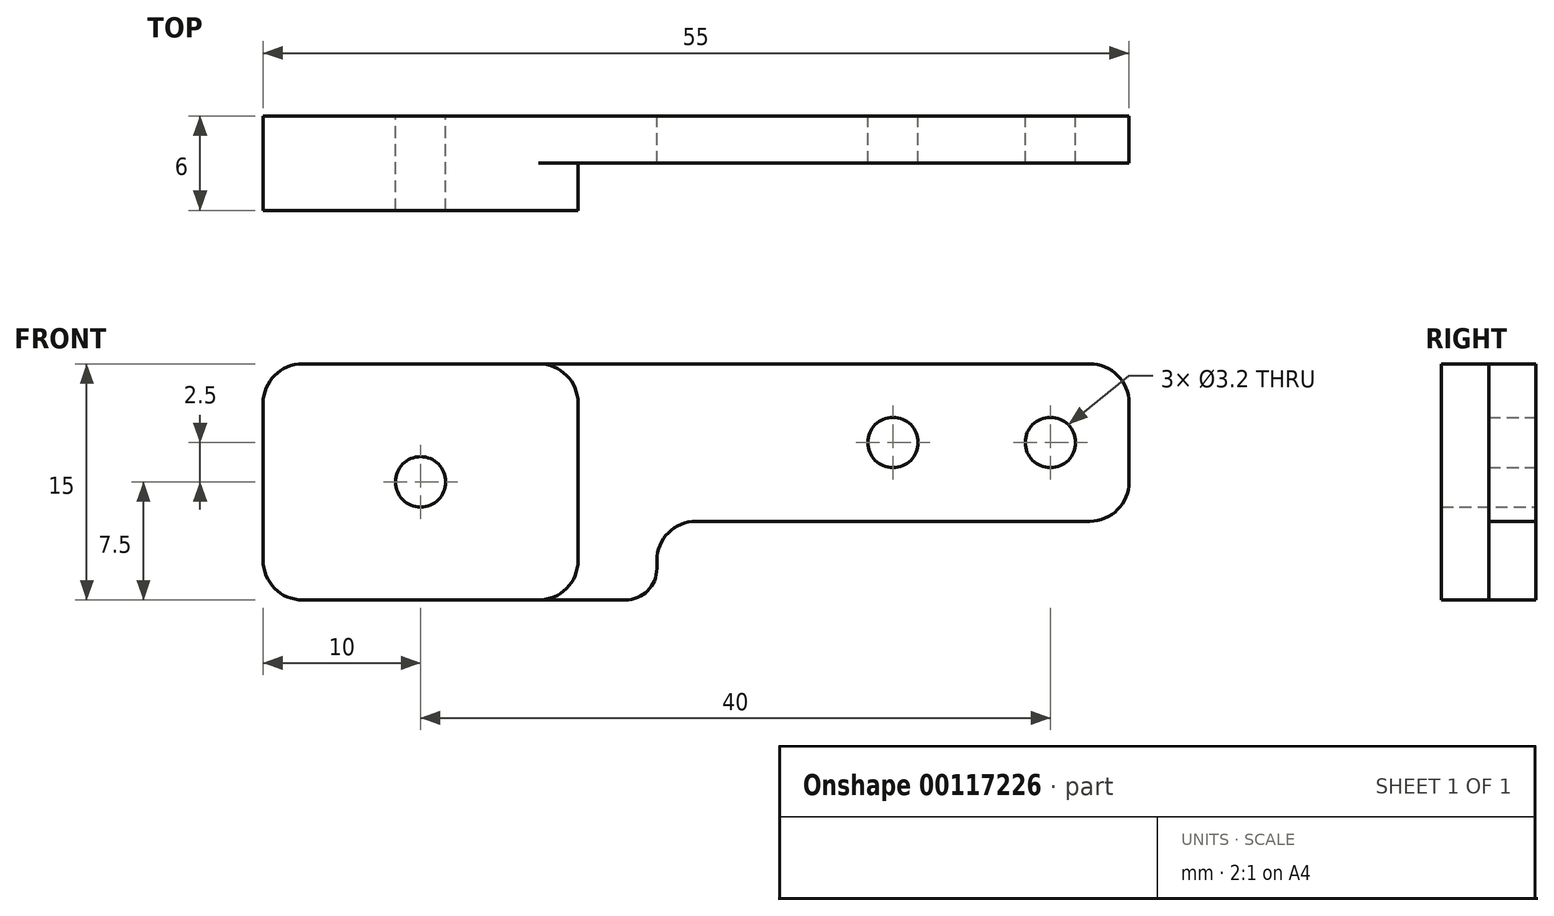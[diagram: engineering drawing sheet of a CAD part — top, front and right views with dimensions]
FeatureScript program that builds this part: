
annotation { "Feature Type Name" : "Feature", "Feature Type Description" : "" }
export const myFeature = defineFeature(function(context is Context, id is Id, definition is map)
    precondition{}
    {
        {
            var Q0;
            Q0=qCreatedBy(makeId("Front.planeOp"),FACE);
            var sketch = newSketch(context, id + "F0", { "sketchPlane" : qUnion([Q0])});
            skLineSegment(sketch, "E0.bottom", {"start": v(-4.5, -7.5) * mm, "end": v(-25, -7.5) * mm});
            skLineSegment(sketch, "E0.top", {"start": v(25, 7.5) * mm, "end": v(-25, 7.5) * mm});
            skLineSegment(sketch, "E0.left", {"start": v(27.5, 0) * mm, "end": v(27.5, 5) * mm});
            skLineSegment(sketch, "E0.right", {"start": v(-27.5, -5) * mm, "end": v(-27.5, 5) * mm});
            skPoint(sketch, "E0.middle", {"position": v(0, 0) * mm});
            skLineSegment(sketch, "E1", {"start": v(-27.5, 0) * mm, "end": v(27.5, 0) * mm, "construction": true});
            skCircle(sketch, "E2", {"center": v(-17.5, 0) * mm, "radius": 1.6 * mm});
            skCircle(sketch, "E3", {"center": v(12.5, 2.5) * mm, "radius": 1.6 * mm});
            skLineSegment(sketch, "E4", {"start": v(12.5, 2.5) * mm, "end": v(32.63, 2.5) * mm, "construction": true});
            skCircle(sketch, "E5", {"center": v(22.5, 2.5) * mm, "radius": 1.6 * mm});
            skLineSegment(sketch, "E6", {"start": v(25, -2.5) * mm, "end": v(0, -2.5) * mm});
            skLineSegment(sketch, "E7", {"start": v(-2.5, -5) * mm, "end": v(-2.5, -5.5) * mm});
            skPoint(sketch, "E8.orphan", {"position": v(27.5, -7.5) * mm});
            skPoint(sketch, "E9.visualSharp", {"position": v(27.5, 7.5) * mm});
            skArc(sketch, "E9.filletArc", {"start": v(27.5, 5) * mm, "mid": v(26.77, 6.77) * mm, "end": v(25, 7.5) * mm});
            skPoint(sketch, "E10.visualSharp", {"position": v(27.5, -2.5) * mm});
            skArc(sketch, "E10.filletArc", {"start": v(25, -2.5) * mm, "mid": v(26.77, -1.77) * mm, "end": v(27.5, 0) * mm});
            skPoint(sketch, "E11.visualSharp", {"position": v(-2.5, -2.5) * mm});
            skArc(sketch, "E11.filletArc", {"start": v(0, -2.5) * mm, "mid": v(-1.77, -3.23) * mm, "end": v(-2.5, -5) * mm});
            skPoint(sketch, "E12.visualSharp", {"position": v(-27.5, 7.5) * mm});
            skArc(sketch, "E12.filletArc", {"start": v(-25, 7.5) * mm, "mid": v(-26.77, 6.77) * mm, "end": v(-27.5, 5) * mm});
            skPoint(sketch, "E13.visualSharp", {"position": v(-27.5, -7.5) * mm});
            skArc(sketch, "E13.filletArc", {"start": v(-27.5, -5) * mm, "mid": v(-26.77, -6.77) * mm, "end": v(-25, -7.5) * mm});
            skPoint(sketch, "E14.visualSharp", {"position": v(-2.5, -7.5) * mm});
            skArc(sketch, "E14.filletArc", {"start": v(-4.5, -7.5) * mm, "mid": v(-3.09, -6.91) * mm, "end": v(-2.5, -5.5) * mm});
            skSolve(sketch);
        }
        {
            var Q0;
            Q0=makeQuery(id+"F0.imprint","IMPRINT",FACE,{"disambiguationData":[TD([[makeQuery(id+"F0.imprint","IMPRINT",EDGE,{"derivedFrom":sQuery(id+"F0.wireOp",EDGE,"E0.bottom")}),-1.0]])]});
            extrude(context, id + "F1", {"entities" : qUnion([Q0]), "depth" : 3 * mm});
        }
        {
            var Q0;
            Q0=makeQuery(id+"F1.opExtrude","CAP_FACE",FACE,{"disambiguationData":[OSD([sQuery(id+"F0.wireOp",EDGE,"E0.bottom"),sQuery(id+"F0.wireOp",EDGE,"E0.top"),sQuery(id+"F0.wireOp",EDGE,"E0.left"),sQuery(id+"F0.wireOp",EDGE,"E0.right"),sQuery(id+"F0.wireOp",EDGE,"E2"),sQuery(id+"F0.wireOp",EDGE,"E3"),sQuery(id+"F0.wireOp",EDGE,"E5"),sQuery(id+"F0.wireOp",EDGE,"E6"),sQuery(id+"F0.wireOp",EDGE,"E7"),sQuery(id+"F0.wireOp",EDGE,"E9.filletArc"),sQuery(id+"F0.wireOp",EDGE,"E10.filletArc"),sQuery(id+"F0.wireOp",EDGE,"E11.filletArc"),sQuery(id+"F0.wireOp",EDGE,"E12.filletArc"),sQuery(id+"F0.wireOp",EDGE,"E13.filletArc"),sQuery(id+"F0.wireOp",EDGE,"E14.filletArc")])],"isStart":false});
            var sketch = newSketch(context, id + "F2", { "sketchPlane" : qUnion([Q0])});
            skLineSegment(sketch, "E15.bottom", {"start": v(-10, -7.5) * mm, "end": v(-25, -7.5) * mm});
            skLineSegment(sketch, "E15.top", {"start": v(-10, 7.5) * mm, "end": v(-25, 7.5) * mm});
            skLineSegment(sketch, "E15.left", {"start": v(-7.5, -5) * mm, "end": v(-7.5, 5) * mm});
            skLineSegment(sketch, "E15.right", {"start": v(-27.5, -5) * mm, "end": v(-27.5, 5) * mm});
            skPoint(sketch, "E15.middle", {"position": v(-17.5, 0) * mm});
            skPoint(sketch, "E16.visualSharp", {"position": v(-27.5, 7.5) * mm});
            skArc(sketch, "E16.filletArc", {"start": v(-25, 7.5) * mm, "mid": v(-26.77, 6.77) * mm, "end": v(-27.5, 5) * mm});
            skPoint(sketch, "E17.visualSharp", {"position": v(-7.5, 7.5) * mm});
            skArc(sketch, "E17.filletArc", {"start": v(-7.5, 5) * mm, "mid": v(-8.23, 6.77) * mm, "end": v(-10, 7.5) * mm});
            skPoint(sketch, "E18.visualSharp", {"position": v(-7.5, -7.5) * mm});
            skArc(sketch, "E18.filletArc", {"start": v(-10, -7.5) * mm, "mid": v(-8.23, -6.77) * mm, "end": v(-7.5, -5) * mm});
            skPoint(sketch, "E19.visualSharp", {"position": v(-27.5, -7.5) * mm});
            skArc(sketch, "E19.filletArc", {"start": v(-27.5, -5) * mm, "mid": v(-26.77, -6.77) * mm, "end": v(-25, -7.5) * mm});
            skCircle(sketch, "E20", {"center": v(-17.5, 0) * mm, "radius": 1.6 * mm});
            skSolve(sketch);
        }
        {
            var Q0;
            Q0=makeQuery(id+"F2.imprint","IMPRINT",FACE,{"disambiguationData":[TD([[makeQuery(id+"F2.imprint","IMPRINT",EDGE,{"derivedFrom":sQuery(id+"F2.wireOp",EDGE,"E15.bottom")}),-1.0]])]});
            extrude(context, id + "F3", {"entities" : qUnion([Q0]), "operationType" : NewBodyOperationType.ADD, "depth" : 3 * mm});
        }
    });
